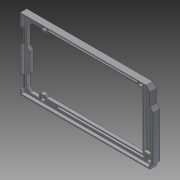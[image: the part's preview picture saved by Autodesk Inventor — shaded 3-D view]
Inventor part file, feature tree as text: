
AUTODESK INVENTOR PART (.ipt)
format: ipt  version: 2012 SP1 (Build 160190100, 190)  size: 296,960 bytes
history: native  units: in
note: dims shown in document units (in); Inventor stores cm internally (conversion verified against a paired STEP export)
features: extrude x5, sketch x5, chamfer x3, projected_geometry x1
ambient origin geometry x8: Origin, YZ Plane, XZ Plane, XY Plane, X Axis, Y Axis, Z Axis, Center Point
feature tree (14):
  extrude  "Extrusion2"  Depth=2.1in
  extrude  "Extrusion3"  Depth=2.0in
  extrude  "Extrusion4"  Depth=1.6in
  extrude  "Extrusion5"  Depth=3.9in
  extrude  "Extrusion7"  Depth=0.15in
  chamfer  "Chamfer3"  Distance=0.008in
  chamfer  "Chamfer5"  Distance=0.1in
  chamfer  "Chamfer6"  Distance=0.029in
  sketch  "Sketch1"  dims[d0=3.8in d1=2.1in]
  sketch  "Sketch2"  dims[d4=3.9in d5=2.0in]
  sketch  "Sketch4"  dims[d6=4.0in d7=1.6in]
  sketch  "Sketch5"  dims[d8=1.5in d9=3.9in]
  projected_geometry  "Projected Loop1"
  sketch  "Sketch7"  dims[d10=0.05in d11=0.15in d15=0.008in d16=0.1in d17=0.0in d18=0.029in d19=3.8in d20=2.1in d21=3.9in d22=2.0in d23=4.0in d24=1.6in d25=1.5in d26=3.9in d27=0.05in d28=0.15in d29=0.008in d30=0.029in d31=0.2in d32=0.1in d33=0.0in d35=0.49in d36=0.1125in d37=1.26in d38=1.74in d39=0.09in d40=0.0in d41=0.0625in d42=1.0in d43=3.65in d44=0.7in d45=3.45in d46=0.0625in d47=2.0312in d48=0.0688in d49=0.085in d50=0.0in d51=0.0in d52=0.475in d54=0.45in d70=0.55in d71=0.1in d72=0.125in d73=2.0in d74=0.125in d75=0.6in d97=0.1in d101=0.1in d102=0.1in d106=0.0625in d107=1.0in d108=2.55in d109=0.7in d110=2.55in d111=0.0625in d112=2.0312in d113=0.0688in d114=0.0in d115=0.475in d116=0.45in d117=0.1in d118=0.1in d119=0.1in d120=0.1in d121=0.1in d122=0.1in d123=0.1in d124=1.0in d125=0.0in d126=0.1in d127=0.125in d128=45.0deg d132=0.1in d133=0.125in d134=45.0deg d135=0.1in d136=0.05in d139=0.015in d140=0.125in d141=45.0deg d142=0.2in d143=0.0in d145=0.25in d146=0.163in d148=3.618in d149=3.65in d150=0.125in d151=0.125in d152=3.55in d153=2.0in d154=0.05in d155=0.1in d156=3.8in]
